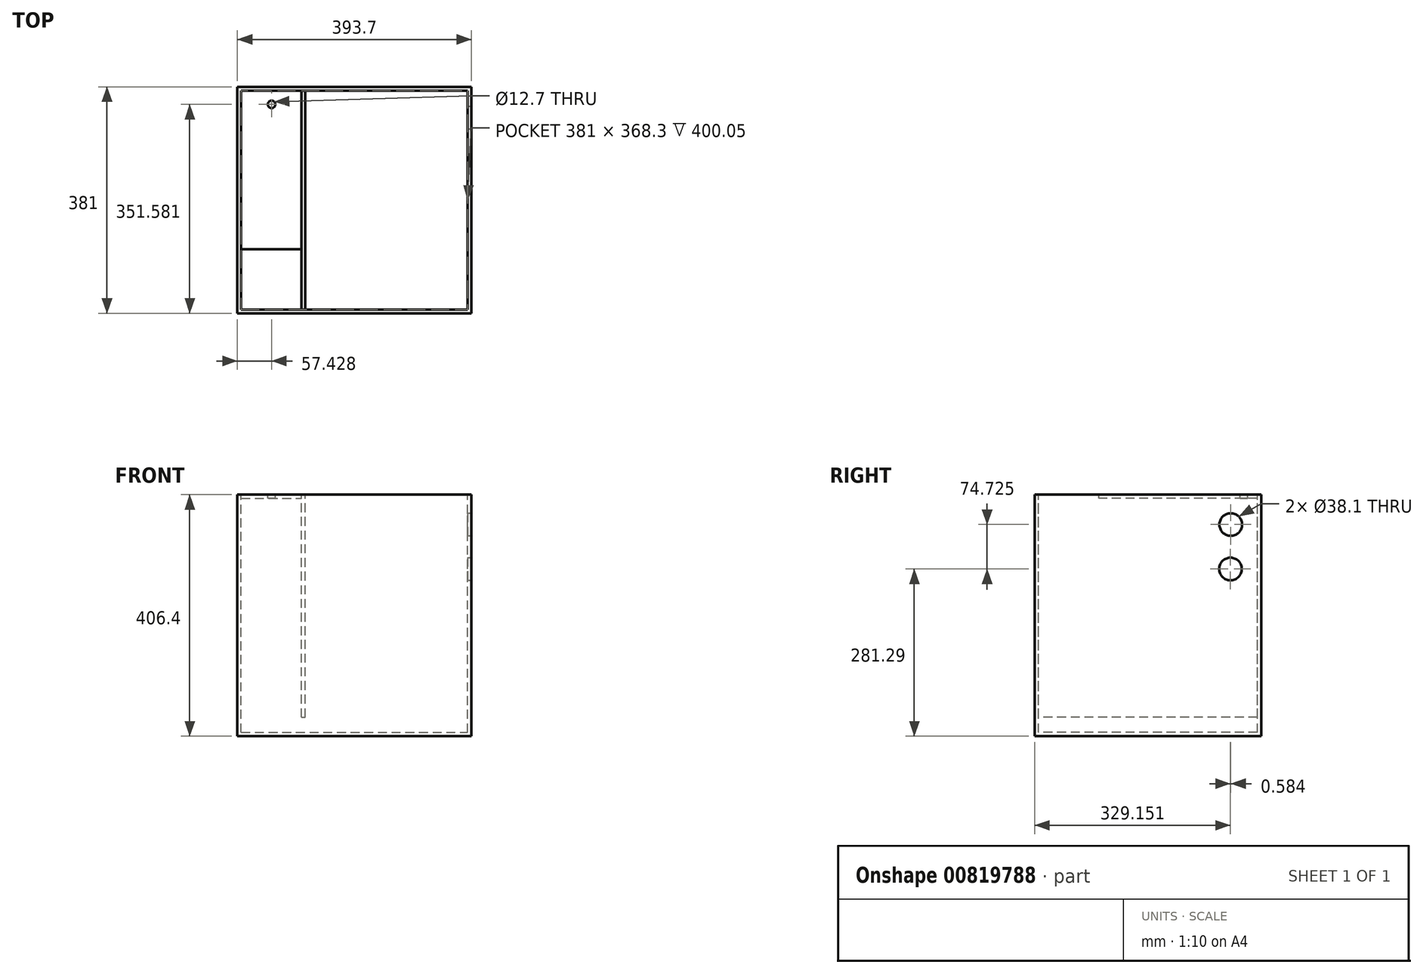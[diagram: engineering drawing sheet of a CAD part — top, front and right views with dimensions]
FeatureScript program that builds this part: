
annotation { "Feature Type Name" : "Feature", "Feature Type Description" : "" }
export const myFeature = defineFeature(function(context is Context, id is Id, definition is map)
    precondition{}
    {
        {
            var Q0;
            Q0=qCreatedBy(makeId("Top.planeOp"),FACE);
            var sketch = newSketch(context, id + "F0", { "sketchPlane" : qUnion([Q0])});
            skLineSegment(sketch, "E0.bottom", {"start": v(-200.82, 188.48) * mm, "end": v(192.88, 188.48) * mm});
            skLineSegment(sketch, "E0.top", {"start": v(-200.82, -192.52) * mm, "end": v(192.88, -192.52) * mm});
            skLineSegment(sketch, "E0.left", {"start": v(-200.82, 188.48) * mm, "end": v(-200.82, -192.52) * mm});
            skLineSegment(sketch, "E0.right", {"start": v(192.88, 188.48) * mm, "end": v(192.88, -192.52) * mm});
            skSolve(sketch);
        }
        {
            var Q0;
            Q0 = qSketchRegion(id + "F0", true);
            extrude(context, id + "F1", {"entities" : qUnion([Q0]), "oppositeDirection" : true, "depth" : 406.4 * mm, "offsetDistance" : 25.4 * mm});
        }
        {
            var Q0;
            Q0=makeQuery(id+"F0.imprint","IMPRINT",FACE,{"disambiguationData":[TD([[makeQuery(id+"F0.imprint","IMPRINT",EDGE,{"derivedFrom":sQuery(id+"F0.wireOp",EDGE,"E0.bottom")}),-1.0]])]});
            var sketch = newSketch(context, id + "F2", { "sketchPlane" : qUnion([Q0])});
            skLineSegment(sketch, "E1.bottom", {"start": v(-194.47, 182.13) * mm, "end": v(186.53, 182.13) * mm});
            skLineSegment(sketch, "E1.top", {"start": v(-194.47, -186.17) * mm, "end": v(186.53, -186.17) * mm});
            skLineSegment(sketch, "E1.left", {"start": v(-194.47, 182.13) * mm, "end": v(-194.47, -186.17) * mm});
            skLineSegment(sketch, "E1.right", {"start": v(186.53, 182.13) * mm, "end": v(186.53, -186.17) * mm});
            skSolve(sketch);
        }
        {
            var Q0;
            Q0 = qSketchRegion(id + "F2", true);
            extrude(context, id + "F3", {"entities" : qUnion([Q0]), "operationType" : NewBodyOperationType.REMOVE, "oppositeDirection" : true, "depth" : 400.05 * mm, "offsetDistance" : 25.4 * mm});
        }
        {
            var Q0;
            Q0=makeQuery(id+"F0.imprint","IMPRINT",FACE,{"disambiguationData":[TD([[makeQuery(id+"F0.imprint","IMPRINT",EDGE,{"derivedFrom":sQuery(id+"F0.wireOp",EDGE,"E0.bottom")}),-1.0]])]});
            var sketch = newSketch(context, id + "F4", { "sketchPlane" : qUnion([Q0])});
            skLineSegment(sketch, "E2.bottom", {"start": v(-92.87, 182.13) * mm, "end": v(-86.52, 182.13) * mm});
            skLineSegment(sketch, "E2.top", {"start": v(-92.87, -186.17) * mm, "end": v(-86.52, -186.17) * mm});
            skLineSegment(sketch, "E2.left", {"start": v(-92.87, 182.13) * mm, "end": v(-92.87, -186.17) * mm});
            skLineSegment(sketch, "E2.right", {"start": v(-86.52, 182.13) * mm, "end": v(-86.52, -186.17) * mm});
            skSolve(sketch);
        }
        {
            var Q0;
            Q0 = qSketchRegion(id + "F4", true);
            extrude(context, id + "F5", {"entities" : qUnion([Q0]), "oppositeDirection" : true, "depth" : 374.65 * mm, "offsetDistance" : 25.4 * mm});
        }
        {
            var Q0;
            Q0=makeQuery(id+"F0.imprint","IMPRINT",FACE,{"disambiguationData":[TD([[makeQuery(id+"F0.imprint","IMPRINT",EDGE,{"derivedFrom":sQuery(id+"F0.wireOp",EDGE,"E0.bottom")}),-1.0]])]});
            var sketch = newSketch(context, id + "F6", { "sketchPlane" : qUnion([Q0])});
            skLineSegment(sketch, "E3.bottom", {"start": v(-194.47, 182.13) * mm, "end": v(-92.87, 182.13) * mm});
            skLineSegment(sketch, "E3.top", {"start": v(-194.47, -84.57) * mm, "end": v(-92.87, -84.57) * mm});
            skLineSegment(sketch, "E3.left", {"start": v(-194.47, 182.13) * mm, "end": v(-194.47, -84.57) * mm});
            skLineSegment(sketch, "E3.right", {"start": v(-92.87, 182.13) * mm, "end": v(-92.87, -84.57) * mm});
            skSolve(sketch);
        }
        {
            var Q0;
            Q0 = qSketchRegion(id + "F6", true);
            extrude(context, id + "F7", {"entities" : qUnion([Q0]), "oppositeDirection" : true, "depth" : 6.35 * mm, "offsetDistance" : 25.4 * mm});
        }
        {
            var Q0;
            Q0=makeQuery(id+"F0.imprint","IMPRINT",FACE,{"disambiguationData":[TD([[makeQuery(id+"F0.imprint","IMPRINT",EDGE,{"derivedFrom":sQuery(id+"F0.wireOp",EDGE,"E0.bottom")}),-1.0]])]});
            var sketch = newSketch(context, id + "F8", { "sketchPlane" : qUnion([Q0])});
            skCircle(sketch, "E4", {"center": v(-143.4, 159.06) * mm, "radius": 6.35 * mm});
            skSolve(sketch);
        }
        {
            var Q0;
            Q0 = qSketchRegion(id + "F8", true);
            extrude(context, id + "F9", {"entities" : qUnion([Q0]), "operationType" : NewBodyOperationType.REMOVE, "oppositeDirection" : true, "depth" : 6.35 * mm, "offsetDistance" : 25.4 * mm});
        }
        {
            var Q0;
            Q0=makeQuery(id+"F1.opExtrude","SWEPT_FACE",FACE,{"disambiguationData":[OSD([sQuery(id+"F0.wireOp",EDGE,"E0.right")])]});
            var sketch = newSketch(context, id + "F10", { "sketchPlane" : qUnion([Q0])});
            skCircle(sketch, "E5", {"center": v(136.63, -125.11) * mm, "radius": 19.05 * mm});
            skSolve(sketch);
        }
        {
            var Q0;
            Q0 = qSketchRegion(id + "F10", true);
            extrude(context, id + "F11", {"entities" : qUnion([Q0]), "operationType" : NewBodyOperationType.REMOVE, "oppositeDirection" : true, "depth" : 6.35 * mm, "offsetDistance" : 25.4 * mm});
        }
        {
            var Q0;
            Q0=makeQuery(id+"F1.opExtrude","SWEPT_FACE",FACE,{"disambiguationData":[OSD([sQuery(id+"F0.wireOp",EDGE,"E0.right")])]});
            var sketch = newSketch(context, id + "F12", { "sketchPlane" : qUnion([Q0])});
            skCircle(sketch, "E6", {"center": v(137.21, -50.39) * mm, "radius": 19.05 * mm});
            skSolve(sketch);
        }
        {
            var Q0;
            Q0 = qSketchRegion(id + "F12", true);
            extrude(context, id + "F13", {"entities" : qUnion([Q0]), "operationType" : NewBodyOperationType.REMOVE, "oppositeDirection" : true, "depth" : 6.35 * mm, "offsetDistance" : 25.4 * mm});
        }
    });
